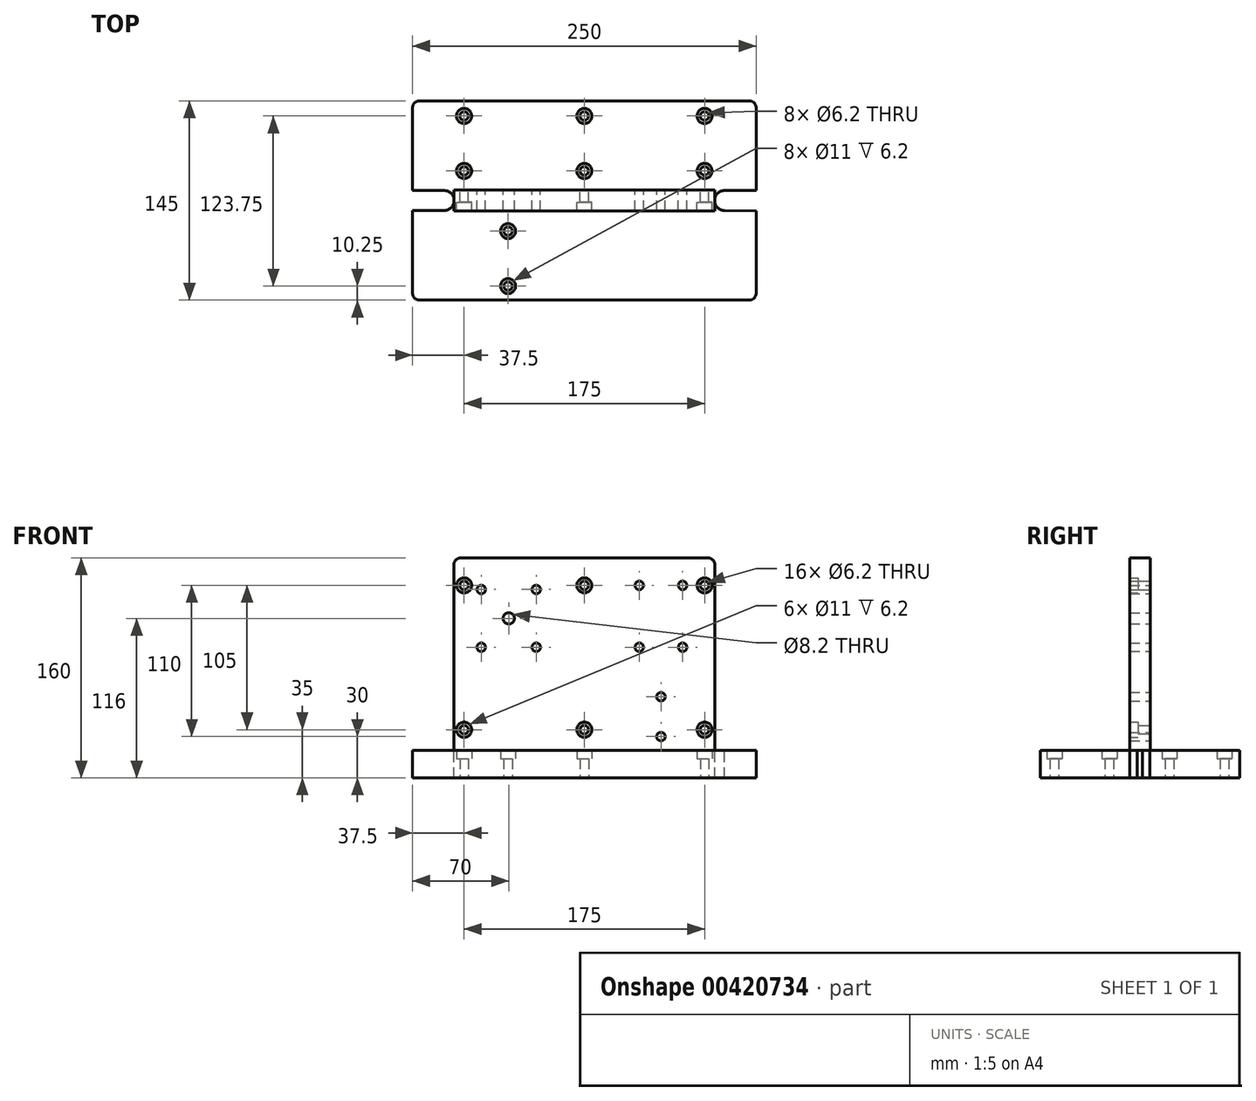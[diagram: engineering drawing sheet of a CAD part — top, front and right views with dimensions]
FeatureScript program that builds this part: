
annotation { "Feature Type Name" : "Feature", "Feature Type Description" : "" }
export const myFeature = defineFeature(function(context is Context, id is Id, definition is map)
    precondition{}
    {
        {
            var Q0;
            Q0=qCreatedBy(makeId("Front.planeOp"),FACE);
            var sketch = newSketch(context, id + "F0", { "sketchPlane" : qUnion([Q0])});
            skLineSegment(sketch, "E0", {"start": v(0, 0) * mm, "end": v(0, 140) * mm});
            skLineSegment(sketch, "E1", {"start": v(0, 140) * mm, "end": v(190, 140) * mm});
            skLineSegment(sketch, "E2", {"start": v(190, 140) * mm, "end": v(190, 0) * mm});
            skLineSegment(sketch, "E3", {"start": v(190, 0) * mm, "end": v(0, 0) * mm});
            skLineSegment(sketch, "E4", {"start": v(0, 0) * mm, "end": v(7.5, 0) * mm});
            skLineSegment(sketch, "E5", {"start": v(7.5, 0) * mm, "end": v(7.5, 15) * mm});
            skLineSegment(sketch, "E6", {"start": v(7.5, 15) * mm, "end": v(7.5, 120) * mm});
            skLineSegment(sketch, "E7", {"start": v(0, 0) * mm, "end": v(20, 0) * mm});
            skLineSegment(sketch, "E8", {"start": v(20, 0) * mm, "end": v(20, 75) * mm});
            skLineSegment(sketch, "E9", {"start": v(20, 75) * mm, "end": v(60, 75) * mm});
            skLineSegment(sketch, "E10", {"start": v(150.75, 75) * mm, "end": v(135, 75) * mm});
            skLineSegment(sketch, "E11.MirrorCS", {"start": v(150.75, 75) * mm, "end": v(166.5, 75) * mm});
            skLineSegment(sketch, "E12.MirrorCS", {"start": v(150.75, 120) * mm, "end": v(135, 120) * mm});
            skLineSegment(sketch, "E13.MirrorCS", {"start": v(150.75, 120) * mm, "end": v(166.5, 120) * mm});
            skLineSegment(sketch, "E14", {"start": v(95, 140) * mm, "end": v(95, 132.56) * mm});
            skLineSegment(sketch, "E15.MirrorCS", {"start": v(182.5, 15) * mm, "end": v(182.5, 120) * mm});
            skPoint(sketch, "E16.endSnap0", {"position": v(40, 75) * mm});
            skLineSegment(sketch, "E17", {"start": v(135, 75) * mm, "end": v(135, 0) * mm});
            skLineSegment(sketch, "E18", {"start": v(135, 75) * mm, "end": v(135, 120) * mm});
            skLineSegment(sketch, "E19", {"start": v(20, 117) * mm, "end": v(60, 117) * mm});
            skLineSegment(sketch, "E20", {"start": v(40, 117) * mm, "end": v(40, 96) * mm});
            skPoint(sketch, "E20.endSnap0", {"position": v(20, 96) * mm});
            skLineSegment(sketch, "E21", {"start": v(20, 75) * mm, "end": v(20, 117) * mm});
            skLineSegment(sketch, "E22", {"start": v(60, 75) * mm, "end": v(135, 75) * mm});
            skLineSegment(sketch, "E23", {"start": v(150.75, 75) * mm, "end": v(150.75, 0) * mm});
            skLineSegment(sketch, "E24", {"start": v(150.75, 0) * mm, "end": v(150.75, 10) * mm});
            skLineSegment(sketch, "E25", {"start": v(150.75, 10) * mm, "end": v(150.75, 39) * mm});
            skLineSegment(sketch, "E26", {"start": v(7.5, 120) * mm, "end": v(95, 120) * mm});
            skLineSegment(sketch, "E27", {"start": v(7.5, 15) * mm, "end": v(95, 15) * mm});
            skPoint(sketch, "E27.endSnap0", {"position": v(95, 0) * mm});
            skSolve(sketch);
        }
        {
            var Q0;
            {var subQ1=sQuery(id+"F0.wireOp",EDGE,"E0");Q0=makeQuery(id+"F0.imprint","IMPRINT",FACE,{"disambiguationData":[TD([[makeQuery(id+"F0.imprint","IMPRINT",EDGE,{"derivedFrom":subQ1}),-1.0]])]});}
            var Q1;
            {var subQ0=sQuery(id+"F0.wireOp",EDGE,"E8");Q1=makeQuery(id+"F0.imprint","IMPRINT",FACE,{"disambiguationData":[TD([[makeQuery(id+"F0.imprint","IMPRINT",EDGE,{"derivedFrom":subQ0}),-1.0]])]});}
            var Q2;
            Q2=makeQuery(id+"F0.imprint","IMPRINT",FACE,{"disambiguationData":[TD([[makeQuery(id+"F0.imprint","IMPRINT",EDGE,{"derivedFrom":sQuery(id+"F0.wireOp",EDGE,"E10")}),1.0]])]});
            var Q3;
            {var subQ0=sQuery(id+"F0.wireOp",EDGE,"E5");Q3=makeQuery(id+"F0.imprint","IMPRINT",FACE,{"disambiguationData":[TD([[makeQuery(id+"F0.imprint","IMPRINT",EDGE,{"derivedFrom":subQ0}),-1.0]])]});}
            extrude(context, id + "F1", {"entities" : qUnion([Q0, Q1, Q2, Q3]), "oppositeDirection" : true, "depth" : 15 * mm});
        }
        {
            var Q0;
            Q0=sQuery(id+"F0.wireOp",VERTEX,"34mdLmB8-NYQB-JZsu-nvt2-5NjCd41thSz9.end");
            var Q1;
            Q1=sQuery(id+"F0.wireOp",VERTEX,"34mdLmB8-NYQB-JZsu-nvt2-5NjCd41thSz9.start");
            var Q2;
            Q2=sQuery(id+"F0.wireOp",VERTEX,"sVGx68N3-lHx0-SeU1-Wsyp-G0nHdIK6jY9Y.start");
            var Q3;
            Q3=sQuery(id+"F0.wireOp",VERTEX,"E9.start");
            var Q4;
            Q4=sQuery(id+"F0.wireOp",VERTEX,"E10.end");
            var Q5;
            Q5=sQuery(id+"F0.wireOp",VERTEX,"E11.MirrorCS.end");
            var Q6;
            Q6=sQuery(id+"F0.wireOp",VERTEX,"E13.MirrorCS.end");
            var Q7;
            Q7=sQuery(id+"F0.wireOp",VERTEX,"E12.MirrorCS.end");
            var Q8;
            Q8=sQuery(id+"F0.wireOp",VERTEX,"E21.end");
            var Q9;
            Q9=sQuery(id+"F0.wireOp",VERTEX,"E9.end");
            var Q10;
            Q10=sQuery(id+"F0.wireOp",VERTEX,"E19.end");
            var Q11;
            Q11=sQuery(id+"F0.wireOp",VERTEX,"BHiPy3Hi-77jz-DfpR-rVcZ-a86G7vlrGmI7.start");
            var Q12;
            Q12=sQuery(id+"F0.wireOp",VERTEX,"BHiPy3Hi-77jz-DfpR-rVcZ-a86G7vlrGmI7.end");
            var Q13;
            Q13=makeQuery(id+"F1.opExtrude","SWEPT_BODY",BODY,{"disambiguationData":[OSD([sQuery(id+"F0.wireOp",EDGE,"E0"),sQuery(id+"F0.wireOp",EDGE,"E1"),sQuery(id+"F0.wireOp",EDGE,"E2"),sQuery(id+"F0.wireOp",EDGE,"E3"),sQuery(id+"F0.wireOp",EDGE,"E7")])]});
            hole(context, id + "F2", {"style" : HoleStyle.SIMPLE, "endStyle" : HoleEndStyle.THROUGH, "holeDiameter" : 6.2 * mm, "isTappedThrough" : true, "tappedDepth" : 12 * mm, "tapClearance" : 3, "locations" : qUnion([Q0, Q1, Q2, Q3, Q4, Q5, Q6, Q7, Q8, Q9, Q10, Q11, Q12]), "scope" : qUnion([Q13]), "startStyle" : HoleStartStyle.PART});
        }
        {
            var Q0;
            Q0=sQuery(id+"F0.wireOp",VERTEX,"D5USdWYK-PwDX-QjbQ-VQpl-hIfxQhAHhKJj.end");
            var Q1;
            Q1=sQuery(id+"F0.wireOp",VERTEX,"E20.end");
            var Q2;
            Q2=makeQuery(id+"F1.opExtrude","SWEPT_BODY",BODY,{"disambiguationData":[OSD([sQuery(id+"F0.wireOp",EDGE,"E0"),sQuery(id+"F0.wireOp",EDGE,"E1"),sQuery(id+"F0.wireOp",EDGE,"E2"),sQuery(id+"F0.wireOp",EDGE,"E3"),sQuery(id+"F0.wireOp",EDGE,"E7")])]});
            hole(context, id + "F3", {"style" : HoleStyle.SIMPLE, "endStyle" : HoleEndStyle.THROUGH, "holeDiameter" : 8.2 * mm, "isTappedThrough" : true, "tappedDepth" : 12 * mm, "tapClearance" : 3, "locations" : qUnion([Q0, Q1]), "scope" : qUnion([Q2]), "startStyle" : HoleStartStyle.PART});
        }
        {
            var Q0;
            Q0=makeQuery(id+"F1.opExtrude","SWEPT_FACE",FACE,{"disambiguationData":[OSD([sQuery(id+"F0.wireOp",EDGE,"E3"),sQuery(id+"F0.wireOp",EDGE,"E7")])]});
            var sketch = newSketch(context, id + "F4", { "sketchPlane" : qUnion([Q0])});
            skLineSegment(sketch, "E28", {"start": v(95, 0) * mm, "end": v(95, 65) * mm});
            skLineSegment(sketch, "E29", {"start": v(95, 65) * mm, "end": v(-30, 65) * mm});
            skLineSegment(sketch, "E30", {"start": v(-30, 65) * mm, "end": v(-30, -7.5) * mm});
            skPoint(sketch, "E30.endSnap0", {"position": v(0, -7.5) * mm});
            skLineSegment(sketch, "E31.MirrorCS", {"start": v(95, 65) * mm, "end": v(220, 65) * mm});
            skLineSegment(sketch, "E32.MirrorCS", {"start": v(220, 65) * mm, "end": v(220, -7.5) * mm});
            skLineSegment(sketch, "E33.MirrorCS", {"start": v(-30, -80) * mm, "end": v(-30, -7.5) * mm});
            skLineSegment(sketch, "E34.MirrorCS", {"start": v(95, -80) * mm, "end": v(-30, -80) * mm});
            skLineSegment(sketch, "E35.MirrorCS", {"start": v(95, -80) * mm, "end": v(220, -80) * mm});
            skLineSegment(sketch, "E36.MirrorCS", {"start": v(220, -80) * mm, "end": v(220, -7.5) * mm});
            skLineSegment(sketch, "E37", {"start": v(-30, -7.5) * mm, "end": v(-14.25, -7.5) * mm});
            skArc(sketch, "E38", {"start": v(-7, -14.75) * mm, "mid": v(0.25, -7.5) * mm, "end": v(-7, -0.25) * mm});
            skLineSegment(sketch, "E39", {"start": v(-7, -7.5) * mm, "end": v(-7, -14.75) * mm});
            skLineSegment(sketch, "E40", {"start": v(-7, -14.75) * mm, "end": v(-30, -14.75) * mm});
            skLineSegment(sketch, "E41.MirrorCS", {"start": v(-7, -0.25) * mm, "end": v(-30, -0.25) * mm});
            skArc(sketch, "E42.MirrorCS", {"start": v(197, -14.75) * mm, "mid": v(189.75, -7.5) * mm, "end": v(197, -0.25) * mm});
            skLineSegment(sketch, "E43.MirrorCS", {"start": v(197, -14.75) * mm, "end": v(220, -14.75) * mm});
            skLineSegment(sketch, "E44", {"start": v(7.5, -29) * mm, "end": v(7.5, -29) * mm});
            skLineSegment(sketch, "E45", {"start": v(7.5, -29) * mm, "end": v(7.5, -69) * mm});
            skLineSegment(sketch, "E46", {"start": v(197, -0.25) * mm, "end": v(220, 0) * mm});
            skLineSegment(sketch, "E47", {"start": v(7.5, -69) * mm, "end": v(182.5, -69) * mm});
            skLineSegment(sketch, "E48", {"start": v(182.5, -15) * mm, "end": v(182.5, 0) * mm});
            skLineSegment(sketch, "E49", {"start": v(182.5, 0) * mm, "end": v(182.5, -15) * mm});
            skCircle(sketch, "E50", {"center": v(7.5, -69) * mm, "radius": 3 * mm});
            skCircle(sketch, "E51", {"center": v(7.5, -69) * mm, "radius": 6 * mm});
            skCircle(sketch, "E52.MirrorC", {"center": v(182.5, -69) * mm, "radius": 6 * mm});
            skCircle(sketch, "E53.MirrorC", {"center": v(182.5, -69) * mm, "radius": 3 * mm});
            skLineSegment(sketch, "E54", {"start": v(7.5, -49) * mm, "end": v(29.1, -49) * mm});
            skPoint(sketch, "E54.endSnap0", {"position": v(7.5, -49) * mm});
            skCircle(sketch, "E55.MirrorC", {"center": v(7.5, -29) * mm, "radius": 6 * mm});
            skCircle(sketch, "E56.MirrorC", {"center": v(7.5, -29) * mm, "radius": 3 * mm});
            skCircle(sketch, "E57.MirrorC", {"center": v(182.5, -29) * mm, "radius": 6 * mm});
            skCircle(sketch, "E58.MirrorC", {"center": v(182.5, -29) * mm, "radius": 3 * mm});
            skLineSegment(sketch, "E59", {"start": v(95, -69) * mm, "end": v(95, -29) * mm});
            skLineSegment(sketch, "E60", {"start": v(7.5, -29) * mm, "end": v(7.5, 0) * mm});
            skLineSegment(sketch, "E61", {"start": v(7.5, 0) * mm, "end": v(39.5, 0) * mm});
            skLineSegment(sketch, "E62", {"start": v(39.5, 0) * mm, "end": v(39.5, -29) * mm});
            skLineSegment(sketch, "E63", {"start": v(39.5, -29) * mm, "end": v(39.5, 14.75) * mm});
            skLineSegment(sketch, "E64", {"start": v(39.5, 14.75) * mm, "end": v(39.5, 54.75) * mm});
            skSolve(sketch);
        }
        {
            var Q0;
            {var subQ0=sQuery(id+"F4.wireOp",EDGE,"E51");var subQ1=sQuery(id+"F4.wireOp",EDGE,"E45");var subQ2=makeQuery(id+"F4.imprint","INTERSECT",VERTEX,{"derivedFrom":[subQ1,subQ0]});Q0=makeQuery(id+"F4.imprint","IMPRINT",FACE,{"disambiguationData":[TD([[makeQuery(id+"F4.imprint","IMPRINT",EDGE,{"disambiguationData":[TD([[subQ2,-1.0]])],"derivedFrom":subQ1}),-1.0]])]});}
            var Q1;
            {var subQ0=sQuery(id+"F4.wireOp",EDGE,"E51");var subQ1=sQuery(id+"F4.wireOp",EDGE,"E45");var subQ2=makeQuery(id+"F4.imprint","INTERSECT",VERTEX,{"derivedFrom":[subQ1,subQ0]});Q1=makeQuery(id+"F4.imprint","IMPRINT",FACE,{"disambiguationData":[TD([[makeQuery(id+"F4.imprint","IMPRINT",EDGE,{"disambiguationData":[TD([[subQ2,-1.0]])],"derivedFrom":subQ1}),1.0]])]});}
            var Q2;
            Q2=makeQuery(id+"F4.imprint","IMPRINT",FACE,{"disambiguationData":[TD([[makeQuery(id+"F4.imprint","IMPRINT",EDGE,{"derivedFrom":sQuery(id+"F4.wireOp",EDGE,"E52.MirrorC")}),-1.0]])]});
            var Q3;
            {var subQ0=sQuery(id+"F4.wireOp",EDGE,"E51");var subQ1=sQuery(id+"F4.wireOp",EDGE,"E47");var subQ2=makeQuery(id+"F4.imprint","INTERSECT",VERTEX,{"derivedFrom":[subQ1,subQ0]});Q3=makeQuery(id+"F4.imprint","IMPRINT",FACE,{"disambiguationData":[TD([[makeQuery(id+"F4.imprint","IMPRINT",EDGE,{"disambiguationData":[TD([[subQ2,1.0]])],"derivedFrom":subQ1}),-1.0]])]});}
            var Q4;
            {var subQ0=sQuery(id+"F4.wireOp",EDGE,"E51");var subQ1=sQuery(id+"F4.wireOp",EDGE,"E47");var subQ2=makeQuery(id+"F4.imprint","INTERSECT",VERTEX,{"derivedFrom":[subQ1,subQ0]});Q4=makeQuery(id+"F4.imprint","IMPRINT",FACE,{"disambiguationData":[TD([[makeQuery(id+"F4.imprint","IMPRINT",EDGE,{"disambiguationData":[TD([[subQ2,1.0]])],"derivedFrom":subQ1}),-1.0]])]});}
            var Q5;
            {var subQ0=sQuery(id+"F4.wireOp",EDGE,"E51");var subQ1=sQuery(id+"F4.wireOp",EDGE,"E47");var subQ2=makeQuery(id+"F4.imprint","INTERSECT",VERTEX,{"derivedFrom":[subQ1,subQ0]});Q5=makeQuery(id+"F4.imprint","IMPRINT",FACE,{"disambiguationData":[TD([[makeQuery(id+"F4.imprint","IMPRINT",EDGE,{"disambiguationData":[TD([[subQ2,1.0]])],"derivedFrom":subQ1}),1.0]])]});}
            var Q6;
            {var subQ0=sQuery(id+"F4.wireOp",EDGE,"E56.MirrorC");var subQ1=sQuery(id+"F4.wireOp",EDGE,"E45");var subQ2=makeQuery(id+"F4.imprint","INTERSECT",VERTEX,{"derivedFrom":[subQ1,subQ0]});Q6=makeQuery(id+"F4.imprint","IMPRINT",FACE,{"disambiguationData":[TD([[makeQuery(id+"F4.imprint","IMPRINT",EDGE,{"disambiguationData":[TD([[subQ2,-1.0]])],"derivedFrom":subQ1}),1.0]])]});}
            var Q7;
            {var subQ0=sQuery(id+"F4.wireOp",EDGE,"E58.MirrorC");var subQ1=sQuery(id+"F4.wireOp",EDGE,"E49");var subQ2=makeQuery(id+"F4.imprint","INTERSECT",VERTEX,{"derivedFrom":[subQ1,subQ0]});Q7=makeQuery(id+"F4.imprint","IMPRINT",FACE,{"disambiguationData":[TD([[makeQuery(id+"F4.imprint","IMPRINT",EDGE,{"disambiguationData":[TD([[subQ2,-1.0]])],"derivedFrom":subQ1}),-1.0]])]});}
            var Q8;
            {var subQ0=sQuery(id+"F4.wireOp",EDGE,"E56.MirrorC");var subQ1=sQuery(id+"F4.wireOp",EDGE,"mPhaeWDJ-Nzgz-2L0b-y6cd-HvV1nDqMggiO");var subQ2=makeQuery(id+"F4.imprint","INTERSECT",VERTEX,{"derivedFrom":[subQ1,subQ0]});Q8=makeQuery(id+"F4.imprint","IMPRINT",FACE,{"disambiguationData":[TD([[makeQuery(id+"F4.imprint","IMPRINT",EDGE,{"disambiguationData":[TD([[subQ2,-1.0]])],"derivedFrom":subQ1}),-1.0]])]});}
            var Q9;
            {var subQ0=sQuery(id+"F4.wireOp",EDGE,"E56.MirrorC");var subQ1=sQuery(id+"F4.wireOp",EDGE,"mPhaeWDJ-Nzgz-2L0b-y6cd-HvV1nDqMggiO");var subQ2=makeQuery(id+"F4.imprint","INTERSECT",VERTEX,{"derivedFrom":[subQ1,subQ0]});Q9=makeQuery(id+"F4.imprint","IMPRINT",FACE,{"disambiguationData":[TD([[makeQuery(id+"F4.imprint","IMPRINT",EDGE,{"disambiguationData":[TD([[subQ2,-1.0]])],"derivedFrom":subQ1}),1.0]])]});}
            var Q10;
            {var subQ0=sQuery(id+"F4.wireOp",EDGE,"E57.MirrorC");var subQ1=sQuery(id+"F4.wireOp",EDGE,"6e4d2df1-713c-46b8-b697-84e0066bc4920.MirrorCS");var subQ2=makeQuery(id+"F4.imprint","INTERSECT",VERTEX,{"derivedFrom":[subQ1,subQ0]});Q10=makeQuery(id+"F4.imprint","IMPRINT",FACE,{"disambiguationData":[TD([[makeQuery(id+"F4.imprint","IMPRINT",EDGE,{"disambiguationData":[TD([[subQ2,-1.0]])],"derivedFrom":subQ1}),1.0]])]});}
            var Q11;
            {var subQ0=sQuery(id+"F4.wireOp",EDGE,"E57.MirrorC");var subQ1=sQuery(id+"F4.wireOp",EDGE,"6e4d2df1-713c-46b8-b697-84e0066bc4920.MirrorCS");var subQ2=makeQuery(id+"F4.imprint","INTERSECT",VERTEX,{"derivedFrom":[subQ1,subQ0]});Q11=makeQuery(id+"F4.imprint","IMPRINT",FACE,{"disambiguationData":[TD([[makeQuery(id+"F4.imprint","IMPRINT",EDGE,{"disambiguationData":[TD([[subQ2,-1.0]])],"derivedFrom":subQ1}),-1.0]])]});}
            var Q12;
            {var subQ18=sQuery(id+"F4.wireOp",EDGE,"E34.MirrorCS");Q12=makeQuery(id+"F4.imprint","IMPRINT",FACE,{"disambiguationData":[TD([[makeQuery(id+"F4.imprint","IMPRINT",EDGE,{"derivedFrom":subQ18}),-1.0]])]});}
            var Q13;
            {var subQ6=sQuery(id+"F4.wireOp",EDGE,"E28");Q13=makeQuery(id+"F4.imprint","IMPRINT",FACE,{"disambiguationData":[TD([[makeQuery(id+"F4.imprint","IMPRINT",EDGE,{"derivedFrom":subQ6}),1.0]])]});}
            var Q14;
            {var subQ8=sQuery(id+"F4.wireOp",EDGE,"E28");Q14=makeQuery(id+"F4.imprint","IMPRINT",FACE,{"disambiguationData":[TD([[makeQuery(id+"F4.imprint","IMPRINT",EDGE,{"derivedFrom":subQ8}),-1.0]])]});}
            var Q15;
            {var subQ0=sQuery(id+"F4.wireOp",EDGE,"E57.MirrorC");var subQ1=sQuery(id+"F4.wireOp",EDGE,"E49");var subQ2=makeQuery(id+"F4.imprint","INTERSECT",VERTEX,{"derivedFrom":[subQ1,subQ0]});Q15=makeQuery(id+"F4.imprint","IMPRINT",FACE,{"disambiguationData":[TD([[makeQuery(id+"F4.imprint","IMPRINT",EDGE,{"disambiguationData":[TD([[subQ2,-1.0]])],"derivedFrom":subQ1}),-1.0]])]});}
            var Q16;
            {var subQ0=sQuery(id+"F4.wireOp",EDGE,"E57.MirrorC");var subQ1=sQuery(id+"F4.wireOp",EDGE,"6e4d2df1-713c-46b8-b697-84e0066bc4920.MirrorCS");var subQ2=makeQuery(id+"F4.imprint","INTERSECT",VERTEX,{"derivedFrom":[subQ1,subQ0]});Q16=makeQuery(id+"F4.imprint","IMPRINT",FACE,{"disambiguationData":[TD([[makeQuery(id+"F4.imprint","IMPRINT",EDGE,{"disambiguationData":[TD([[subQ2,1.0]])],"derivedFrom":subQ0}),-1.0]])]});}
            var Q17;
            {var subQ4=sQuery(id+"F4.wireOp",EDGE,"E55.MirrorC");var subQ12=sQuery(id+"F4.wireOp",EDGE,"mPhaeWDJ-Nzgz-2L0b-y6cd-HvV1nDqMggiO");var subQ14=makeQuery(id+"F4.imprint","INTERSECT",VERTEX,{"derivedFrom":[subQ12,subQ4]});Q17=makeQuery(id+"F4.imprint","IMPRINT",FACE,{"disambiguationData":[TD([[makeQuery(id+"F4.imprint","IMPRINT",EDGE,{"disambiguationData":[TD([[subQ14,1.0]])],"derivedFrom":subQ4}),1.0]])]});}
            var Q18;
            {var subQ0=sQuery(id+"F4.wireOp",EDGE,"E46");Q18=makeQuery(id+"F4.imprint","IMPRINT",FACE,{"disambiguationData":[TD([[makeQuery(id+"F4.imprint","IMPRINT",EDGE,{"derivedFrom":subQ0}),1.0]])]});}
            var Q19;
            {var subQ0=sQuery(id+"F4.wireOp",EDGE,"E41.MirrorCS");Q19=makeQuery(id+"F4.imprint","IMPRINT",FACE,{"disambiguationData":[TD([[makeQuery(id+"F4.imprint","IMPRINT",EDGE,{"derivedFrom":subQ0}),-1.0]])]});}
            extrude(context, id + "F5", {"entities" : qUnion([Q0, Q1, Q2, Q3, Q4, Q5, Q6, Q7, Q8, Q9, Q10, Q11, Q12, Q13, Q14, Q15, Q16, Q17, Q18, Q19]), "depth" : 15 * mm});
        }
        {
            var Q0;
            {var subQ0=sQuery(id+"F4.wireOp",EDGE,"E40");Q0=makeQuery(id+"F4.imprint","IMPRINT",FACE,{"disambiguationData":[TD([[makeQuery(id+"F4.imprint","IMPRINT",EDGE,{"derivedFrom":subQ0}),-1.0]])]});}
            var Q1;
            {var subQ0=sQuery(id+"F4.wireOp",EDGE,"E43.MirrorCS");Q1=makeQuery(id+"F4.imprint","IMPRINT",FACE,{"disambiguationData":[TD([[makeQuery(id+"F4.imprint","IMPRINT",EDGE,{"derivedFrom":subQ0}),1.0]])]});}
            var Q2;
            {var subQ0=sQuery(id+"F4.wireOp",EDGE,"7bHRVPem-sjBZ-Ug8A-odx3-xiCNbKq1Zb4v");var subQ3=sQuery(id+"F4.wireOp",EDGE,"E38");var subQ4=makeQuery(id+"F4.imprint","INTERSECT",VERTEX,{"derivedFrom":[subQ0,subQ3]});Q2=makeQuery(id+"F4.imprint","IMPRINT",FACE,{"disambiguationData":[TD([[makeQuery(id+"F4.imprint","IMPRINT",EDGE,{"disambiguationData":[TD([[subQ4,1.0]])],"derivedFrom":subQ0}),1.0]])]});}
            var Q3;
            {var subQ0=sQuery(id+"F4.wireOp",EDGE,"7bHRVPem-sjBZ-Ug8A-odx3-xiCNbKq1Zb4v");var subQ3=sQuery(id+"F4.wireOp",EDGE,"E38");var subQ4=makeQuery(id+"F4.imprint","INTERSECT",VERTEX,{"derivedFrom":[subQ0,subQ3]});Q3=makeQuery(id+"F4.imprint","IMPRINT",FACE,{"disambiguationData":[TD([[makeQuery(id+"F4.imprint","IMPRINT",EDGE,{"disambiguationData":[TD([[subQ4,1.0]])],"derivedFrom":subQ0}),-1.0]])]});}
            var Q4;
            {var subQ0=sQuery(id+"F4.wireOp",EDGE,"E42.MirrorCS");var subQ1=makeQuery(id+"F1.opExtrude","SWEPT_EDGE",EDGE,{"disambiguationData":[OSD([sQuery(id+"F0.wireOp",EDGE,"E2"),sQuery(id+"F0.wireOp",EDGE,"E3")])]});var subQ2=makeQuery(id+"F4.imprint","INTERSECT",VERTEX,{"disambiguationData":[OD(0.0)],"derivedFrom":[subQ1,subQ0]});Q4=makeQuery(id+"F4.imprint","IMPRINT",FACE,{"disambiguationData":[TD([[makeQuery(id+"F4.imprint","IMPRINT",EDGE,{"disambiguationData":[TD([[subQ2,1.0]])],"derivedFrom":subQ0}),-1.0]])]});}
            extrude(context, id + "F6", {"entities" : qUnion([Q0, Q1, Q2, Q3, Q4]), "operationType" : NewBodyOperationType.REMOVE, "depth" : 25 * mm});
        }
        {
            var Q0;
            Q0=makeQuery(id+"F5.opExtrude","CAP_EDGE",EDGE,{"disambiguationData":[OSD([sQuery(id+"F4.wireOp",EDGE,"E29"),sQuery(id+"F4.wireOp",EDGE,"E31.MirrorCS")])],"isStart":true});
            var Q1;
            {var subQ0=sQuery(id+"F4.wireOp",EDGE,"E33.MirrorCS");var subQ2=sQuery(id+"F4.wireOp",EDGE,"E30");Q1=makeQuery(id+"F6.boolean.opBoolean","SPLIT",EDGE,{"disambiguationData":[TD([makeQuery(id+"F6.opExtrude","SWEPT_FACE",FACE,{"disambiguationData":[OSD([sQuery(id+"F4.wireOp",EDGE,"E41.MirrorCS")])]})])],"derivedFrom":makeQuery(id+"F5.opExtrude","CAP_EDGE",EDGE,{"disambiguationData":[OSD([subQ2,subQ0])],"isStart":true})});}
            var Q2;
            {var subQ2=sQuery(id+"F4.wireOp",EDGE,"E33.MirrorCS");var subQ3=sQuery(id+"F4.wireOp",EDGE,"E30");Q2=makeQuery(id+"F6.boolean.opBoolean","SPLIT",EDGE,{"disambiguationData":[TD([makeQuery(id+"F6.opExtrude","SWEPT_FACE",FACE,{"disambiguationData":[OSD([sQuery(id+"F4.wireOp",EDGE,"E40")])]})])],"derivedFrom":makeQuery(id+"F5.opExtrude","CAP_EDGE",EDGE,{"disambiguationData":[OSD([subQ3,subQ2])],"isStart":true})});}
            var Q3;
            Q3=makeQuery(id+"F5.opExtrude","CAP_EDGE",EDGE,{"disambiguationData":[OSD([sQuery(id+"F4.wireOp",EDGE,"E34.MirrorCS"),sQuery(id+"F4.wireOp",EDGE,"E35.MirrorCS")])],"isStart":true});
            var Q4;
            {var subQ0=sQuery(id+"F4.wireOp",EDGE,"E36.MirrorCS");var subQ1=sQuery(id+"F4.wireOp",EDGE,"E32.MirrorCS");Q4=makeQuery(id+"F6.boolean.opBoolean","SPLIT",EDGE,{"disambiguationData":[TD([makeQuery(id+"F6.opExtrude","SWEPT_FACE",FACE,{"disambiguationData":[OSD([sQuery(id+"F4.wireOp",EDGE,"6e4d2df1-713c-46b8-b697-84e0066bc4920.MirrorCS")])]})])],"derivedFrom":makeQuery(id+"F5.opExtrude","CAP_EDGE",EDGE,{"disambiguationData":[OSD([subQ1,subQ0])],"isStart":true})});}
            var Q5;
            {var subQ0=sQuery(id+"F4.wireOp",EDGE,"E36.MirrorCS");var subQ3=sQuery(id+"F4.wireOp",EDGE,"E32.MirrorCS");Q5=makeQuery(id+"F6.boolean.opBoolean","SPLIT",EDGE,{"disambiguationData":[TD([makeQuery(id+"F6.opExtrude","SWEPT_FACE",FACE,{"disambiguationData":[OSD([sQuery(id+"F4.wireOp",EDGE,"E43.MirrorCS")])]})])],"derivedFrom":makeQuery(id+"F5.opExtrude","CAP_EDGE",EDGE,{"disambiguationData":[OSD([subQ3,subQ0])],"isStart":true})});}
            var Q6;
            Q6=makeQuery(id+"F5.opExtrude","SWEPT_EDGE",EDGE,{"disambiguationData":[OSD([sQuery(id+"F4.wireOp",EDGE,"E29"),sQuery(id+"F4.wireOp",EDGE,"E30")])]});
            var Q7;
            Q7=makeQuery(id+"F5.opExtrude","SWEPT_EDGE",EDGE,{"disambiguationData":[OSD([sQuery(id+"F4.wireOp",EDGE,"E33.MirrorCS"),sQuery(id+"F4.wireOp",EDGE,"E34.MirrorCS")])]});
            var Q8;
            Q8=makeQuery(id+"F5.opExtrude","SWEPT_EDGE",EDGE,{"disambiguationData":[OSD([sQuery(id+"F4.wireOp",EDGE,"E35.MirrorCS"),sQuery(id+"F4.wireOp",EDGE,"E36.MirrorCS")])]});
            var Q9;
            Q9=makeQuery(id+"F5.opExtrude","SWEPT_EDGE",EDGE,{"disambiguationData":[OSD([sQuery(id+"F4.wireOp",EDGE,"E31.MirrorCS"),sQuery(id+"F4.wireOp",EDGE,"E32.MirrorCS")])]});
            var Q10;
            {var subQ0=sQuery(id+"F4.wireOp",EDGE,"E36.MirrorCS");var subQ1=sQuery(id+"F4.wireOp",EDGE,"E32.MirrorCS");Q10=makeQuery(id+"F6.boolean.opBoolean","SPLIT",EDGE,{"disambiguationData":[TD([makeQuery(id+"F6.opExtrude","SWEPT_FACE",FACE,{"disambiguationData":[OSD([sQuery(id+"F4.wireOp",EDGE,"E46")])]})])],"derivedFrom":makeQuery(id+"F5.opExtrude","CAP_EDGE",EDGE,{"disambiguationData":[OSD([subQ1,subQ0])],"isStart":true})});}
            fillet(context, id + "F7", {"entities" : qUnion([Q0, Q1, Q2, Q3, Q4, Q5, Q6, Q7, Q8, Q9, Q10]), "radius" : 5 * mm, "tangentPropagation" : true, "allowEdgeOverflow" : false});
        }
        {
            var Q0;
            Q0=makeQuery(id+"F1.opExtrude","SWEPT_EDGE",EDGE,{"disambiguationData":[OSD([sQuery(id+"F0.wireOp",EDGE,"E0"),sQuery(id+"F0.wireOp",EDGE,"E1")])]});
            var Q1;
            Q1=makeQuery(id+"F1.opExtrude","SWEPT_EDGE",EDGE,{"disambiguationData":[OSD([sQuery(id+"F0.wireOp",EDGE,"E1"),sQuery(id+"F0.wireOp",EDGE,"E2")])]});
            fillet(context, id + "F8", {"entities" : qUnion([Q0, Q1]), "radius" : 5 * mm, "tangentPropagation" : true, "allowEdgeOverflow" : false});
        }
        {
            var Q0;
            {var subQ13=sQuery(id+"F4.wireOp",EDGE,"E34.MirrorCS");Q0=makeQuery(id+"F4.imprint","IMPRINT",FACE,{"disambiguationData":[TD([[makeQuery(id+"F4.imprint","IMPRINT",EDGE,{"derivedFrom":subQ13}),-1.0]])]});}
            cPlane(context, id + "F9", {"entities" : qUnion([Q0]), "cplaneType" : CPlaneType.OFFSET, "offset" : 10 * mm, "width" : 150 * mm, "height" : 150 * mm});
        }
        {
            var Q0;
            Q0=makeQuery(id+"Fad2b0gEey9Uvx4_2.opExtrude","CAP_FACE",FACE,{"disambiguationData":[OSD([sQuery(id+"F4.wireOp",EDGE,"E50"),sQuery(id+"F4.wireOp",EDGE,"E51")])],"isStart":false});
            var Q1;
            Q1=makeQuery(id+"Fad2b0gEey9Uvx4_2.opExtrude","CAP_FACE",FACE,{"disambiguationData":[OSD([sQuery(id+"F4.wireOp",EDGE,"E52.MirrorC"),sQuery(id+"F4.wireOp",EDGE,"E53.MirrorC")])],"isStart":false});
            var Q2;
            {var subQ0=sQuery(id+"F4.wireOp",EDGE,"E51");var subQ1=sQuery(id+"F4.wireOp",EDGE,"E47");var subQ2=makeQuery(id+"F4.imprint","INTERSECT",VERTEX,{"derivedFrom":[subQ1,subQ0]});Q2=makeQuery(id+"F4.imprint","IMPRINT",FACE,{"disambiguationData":[TD([[makeQuery(id+"F4.imprint","IMPRINT",EDGE,{"disambiguationData":[TD([[subQ2,1.0]])],"derivedFrom":subQ1}),-1.0]])]});}
            var Q3;
            {var subQ0=sQuery(id+"F4.wireOp",EDGE,"E51");var subQ1=sQuery(id+"F4.wireOp",EDGE,"E47");var subQ2=makeQuery(id+"F4.imprint","INTERSECT",VERTEX,{"derivedFrom":[subQ1,subQ0]});Q3=makeQuery(id+"F4.imprint","IMPRINT",FACE,{"disambiguationData":[TD([[makeQuery(id+"F4.imprint","IMPRINT",EDGE,{"disambiguationData":[TD([[subQ2,1.0]])],"derivedFrom":subQ1}),1.0]])]});}
            var Q4;
            {var subQ0=sQuery(id+"F4.wireOp",EDGE,"E56.MirrorC");var subQ1=sQuery(id+"F4.wireOp",EDGE,"E45");var subQ2=makeQuery(id+"F4.imprint","INTERSECT",VERTEX,{"derivedFrom":[subQ1,subQ0]});Q4=makeQuery(id+"F4.imprint","IMPRINT",FACE,{"disambiguationData":[TD([[makeQuery(id+"F4.imprint","IMPRINT",EDGE,{"disambiguationData":[TD([[subQ2,-1.0]])],"derivedFrom":subQ1}),1.0]])]});}
            var Q5;
            {var subQ0=sQuery(id+"F4.wireOp",EDGE,"E55.MirrorC");var subQ1=sQuery(id+"F4.wireOp",EDGE,"mPhaeWDJ-Nzgz-2L0b-y6cd-HvV1nDqMggiO");var subQ2=makeQuery(id+"F4.imprint","INTERSECT",VERTEX,{"derivedFrom":[subQ1,subQ0]});Q5=makeQuery(id+"F4.imprint","IMPRINT",FACE,{"disambiguationData":[TD([[makeQuery(id+"F4.imprint","IMPRINT",EDGE,{"disambiguationData":[TD([[subQ2,-1.0]])],"derivedFrom":subQ1}),-1.0]])]});}
            var Q6;
            {var subQ0=sQuery(id+"F4.wireOp",EDGE,"E58.MirrorC");var subQ1=sQuery(id+"F4.wireOp",EDGE,"E49");var subQ2=makeQuery(id+"F4.imprint","INTERSECT",VERTEX,{"derivedFrom":[subQ1,subQ0]});Q6=makeQuery(id+"F4.imprint","IMPRINT",FACE,{"disambiguationData":[TD([[makeQuery(id+"F4.imprint","IMPRINT",EDGE,{"disambiguationData":[TD([[subQ2,-1.0]])],"derivedFrom":subQ1}),-1.0]])]});}
            var Q7;
            {var subQ0=sQuery(id+"F4.wireOp",EDGE,"E58.MirrorC");var subQ1=sQuery(id+"F4.wireOp",EDGE,"6e4d2df1-713c-46b8-b697-84e0066bc4920.MirrorCS");var subQ2=makeQuery(id+"F4.imprint","INTERSECT",VERTEX,{"derivedFrom":[subQ1,subQ0]});Q7=makeQuery(id+"F4.imprint","IMPRINT",FACE,{"disambiguationData":[TD([[makeQuery(id+"F4.imprint","IMPRINT",EDGE,{"disambiguationData":[TD([[subQ2,-1.0]])],"derivedFrom":subQ1}),-1.0]])]});}
            var Q8;
            {var subQ0=sQuery(id+"F4.wireOp",EDGE,"E58.MirrorC");var subQ1=sQuery(id+"F4.wireOp",EDGE,"6e4d2df1-713c-46b8-b697-84e0066bc4920.MirrorCS");var subQ2=makeQuery(id+"F4.imprint","INTERSECT",VERTEX,{"derivedFrom":[subQ1,subQ0]});Q8=makeQuery(id+"F4.imprint","IMPRINT",FACE,{"disambiguationData":[TD([[makeQuery(id+"F4.imprint","IMPRINT",EDGE,{"disambiguationData":[TD([[subQ2,-1.0]])],"derivedFrom":subQ1}),1.0]])]});}
            var Q9;
            {var subQ0=sQuery(id+"F4.wireOp",EDGE,"E55.MirrorC");var subQ1=sQuery(id+"F4.wireOp",EDGE,"mPhaeWDJ-Nzgz-2L0b-y6cd-HvV1nDqMggiO");var subQ2=makeQuery(id+"F4.imprint","INTERSECT",VERTEX,{"derivedFrom":[subQ1,subQ0]});Q9=makeQuery(id+"F4.imprint","IMPRINT",FACE,{"disambiguationData":[TD([[makeQuery(id+"F4.imprint","IMPRINT",EDGE,{"disambiguationData":[TD([[subQ2,-1.0]])],"derivedFrom":subQ1}),1.0]])]});}
            var Q10;
            Q10=makeQuery(id+"Fad2b0gEey9Uvx4_2.opExtrude","CAP_FACE",FACE,{"disambiguationData":[OSD([sQuery(id+"F4.wireOp",EDGE,"E57.MirrorC"),sQuery(id+"F4.wireOp",EDGE,"E58.MirrorC")])],"isStart":false});
            var Q11;
            Q11=makeQuery(id+"Fad2b0gEey9Uvx4_2.opExtrude","CAP_FACE",FACE,{"disambiguationData":[OSD([sQuery(id+"F4.wireOp",EDGE,"E55.MirrorC"),sQuery(id+"F4.wireOp",EDGE,"E56.MirrorC")])],"isStart":false});
            extrude(context, id + "F10", {"entities" : qUnion([Q0, Q1, Q2, Q3, Q4, Q5, Q6, Q7, Q8, Q9, Q10, Q11]), "operationType" : NewBodyOperationType.REMOVE, "oppositeDirection" : true, "depth" : 18 * mm});
        }
        {
            var Q0;
            Q0=sQuery(id+"F0.wireOp",VERTEX,"E6.end");
            var Q1;
            Q1=sQuery(id+"F0.wireOp",VERTEX,"E6.start");
            var Q2;
            Q2=sQuery(id+"F0.wireOp",VERTEX,"E15.MirrorCS.start");
            var Q3;
            Q3=sQuery(id+"F0.wireOp",VERTEX,"E15.MirrorCS.end");
            var Q4;
            Q4=sQuery(id+"F0.wireOp",VERTEX,"E26.end");
            var Q5;
            Q5=sQuery(id+"F0.wireOp",VERTEX,"E27.end");
            var Q6;
            Q6=makeQuery(id+"F1.opExtrude","SWEPT_BODY",BODY,{"disambiguationData":[OSD([sQuery(id+"F0.wireOp",EDGE,"E0"),sQuery(id+"F0.wireOp",EDGE,"E1"),sQuery(id+"F0.wireOp",EDGE,"E2"),sQuery(id+"F0.wireOp",EDGE,"E3"),sQuery(id+"F0.wireOp",EDGE,"E7")])]});
            hole(context, id + "F11", {"style" : HoleStyle.C_BORE, "endStyle" : HoleEndStyle.THROUGH, "holeDiameter" : 6.2 * mm, "cBoreDiameter" : 11 * mm, "cBoreDepth" : 6.2 * mm, "majorDiameter" : 5 * mm, "isTappedThrough" : true, "tappedDepth" : 12 * mm, "tapClearance" : 3, "locations" : qUnion([Q0, Q1, Q2, Q3, Q4, Q5]), "scope" : qUnion([Q6]), "startStyle" : HoleStartStyle.PART});
        }
        {
            var Q0;
            Q0=makeQuery(id+"F5.opExtrude","SWEPT_BODY",BODY,{"disambiguationData":[OSD([sQuery(id+"F0.wireOp",EDGE,"E3"),sQuery(id+"F0.wireOp",EDGE,"E7"),sQuery(id+"F4.wireOp",EDGE,"E49"),sQuery(id+"F4.wireOp",EDGE,"E58.MirrorC")])]});
            deleteBodies(context, id + "F12", {"entities" : qUnion([Q0])});
        }
        {
            var Q0;
            Q0 = qSketchRegion(id + "F4", true);
            var Q1;
            {var subQ0=sQuery(id+"F4.wireOp",EDGE,"E51");var subQ1=sQuery(id+"F4.wireOp",EDGE,"E47");var subQ2=makeQuery(id+"F4.imprint","INTERSECT",VERTEX,{"derivedFrom":[subQ1,subQ0]});Q1=makeQuery(id+"F4.imprint","IMPRINT",FACE,{"disambiguationData":[TD([[makeQuery(id+"F4.imprint","IMPRINT",EDGE,{"disambiguationData":[TD([[subQ2,1.0]])],"derivedFrom":subQ1}),-1.0]])]});}
            var Q2;
            {var subQ0=sQuery(id+"F4.wireOp",EDGE,"E45");var subQ1=sQuery(id+"F4.wireOp",EDGE,"E47");var subQ2=makeQuery(id+"F4.imprint","INTERSECT",VERTEX,{"derivedFrom":[subQ1,subQ0]});Q2=makeQuery(id+"F4.imprint","IMPRINT",FACE,{"disambiguationData":[TD([[makeQuery(id+"F4.imprint","IMPRINT",EDGE,{"disambiguationData":[TD([[subQ2,-1.0]])],"derivedFrom":subQ1}),-1.0]])]});}
            var Q3;
            Q3=makeQuery(id+"F4.imprint","IMPRINT",FACE,{"disambiguationData":[TD([[makeQuery(id+"F4.imprint","IMPRINT",EDGE,{"derivedFrom":sQuery(id+"F4.wireOp",EDGE,"E52.MirrorC")}),-1.0]])]});
            var Q4;
            Q4=makeQuery(id+"F4.imprint","IMPRINT",FACE,{"disambiguationData":[TD([[makeQuery(id+"F4.imprint","IMPRINT",EDGE,{"derivedFrom":sQuery(id+"F4.wireOp",EDGE,"E53.MirrorC")}),-1.0]])]});
            var Q5;
            {var subQ0=sQuery(id+"F4.wireOp",EDGE,"E56.MirrorC");var subQ1=sQuery(id+"F4.wireOp",EDGE,"E45");var subQ2=makeQuery(id+"F4.imprint","INTERSECT",VERTEX,{"derivedFrom":[subQ1,subQ0]});Q5=makeQuery(id+"F4.imprint","IMPRINT",FACE,{"disambiguationData":[TD([[makeQuery(id+"F4.imprint","IMPRINT",EDGE,{"disambiguationData":[TD([[subQ2,-1.0]])],"derivedFrom":subQ1}),1.0]])]});}
            var Q6;
            {var subQ1=sQuery(id+"F4.wireOp",EDGE,"mPhaeWDJ-Nzgz-2L0b-y6cd-HvV1nDqMggiO");var subQ3=sQuery(id+"F4.wireOp",EDGE,"E56.MirrorC");var subQ4=makeQuery(id+"F4.imprint","INTERSECT",VERTEX,{"derivedFrom":[subQ1,subQ3]});Q6=makeQuery(id+"F4.imprint","IMPRINT",FACE,{"disambiguationData":[TD([[makeQuery(id+"F4.imprint","IMPRINT",EDGE,{"disambiguationData":[TD([[subQ4,1.0]])],"derivedFrom":subQ3}),-1.0]])]});}
            var Q7;
            {var subQ0=sQuery(id+"F4.wireOp",EDGE,"E56.MirrorC");var subQ1=sQuery(id+"F4.wireOp",EDGE,"mPhaeWDJ-Nzgz-2L0b-y6cd-HvV1nDqMggiO");var subQ2=makeQuery(id+"F4.imprint","INTERSECT",VERTEX,{"derivedFrom":[subQ1,subQ0]});Q7=makeQuery(id+"F4.imprint","IMPRINT",FACE,{"disambiguationData":[TD([[makeQuery(id+"F4.imprint","IMPRINT",EDGE,{"disambiguationData":[TD([[subQ2,-1.0]])],"derivedFrom":subQ1}),1.0]])]});}
            var Q8;
            {var subQ0=sQuery(id+"F4.wireOp",EDGE,"E56.MirrorC");var subQ1=sQuery(id+"F4.wireOp",EDGE,"mPhaeWDJ-Nzgz-2L0b-y6cd-HvV1nDqMggiO");var subQ2=makeQuery(id+"F4.imprint","INTERSECT",VERTEX,{"derivedFrom":[subQ1,subQ0]});Q8=makeQuery(id+"F4.imprint","IMPRINT",FACE,{"disambiguationData":[TD([[makeQuery(id+"F4.imprint","IMPRINT",EDGE,{"disambiguationData":[TD([[subQ2,-1.0]])],"derivedFrom":subQ1}),-1.0]])]});}
            var Q9;
            {var subQ0=sQuery(id+"F4.wireOp",EDGE,"E57.MirrorC");var subQ1=sQuery(id+"F4.wireOp",EDGE,"6e4d2df1-713c-46b8-b697-84e0066bc4920.MirrorCS");var subQ2=makeQuery(id+"F4.imprint","INTERSECT",VERTEX,{"derivedFrom":[subQ1,subQ0]});Q9=makeQuery(id+"F4.imprint","IMPRINT",FACE,{"disambiguationData":[TD([[makeQuery(id+"F4.imprint","IMPRINT",EDGE,{"disambiguationData":[TD([[subQ2,-1.0]])],"derivedFrom":subQ1}),-1.0]])]});}
            var Q10;
            {var subQ0=sQuery(id+"F4.wireOp",EDGE,"6e4d2df1-713c-46b8-b697-84e0066bc4920.MirrorCS");var subQ3=sQuery(id+"F4.wireOp",EDGE,"E58.MirrorC");var subQ4=makeQuery(id+"F4.imprint","INTERSECT",VERTEX,{"derivedFrom":[subQ0,subQ3]});Q10=makeQuery(id+"F4.imprint","IMPRINT",FACE,{"disambiguationData":[TD([[makeQuery(id+"F4.imprint","IMPRINT",EDGE,{"disambiguationData":[TD([[subQ4,-1.0]])],"derivedFrom":subQ3}),1.0]])]});}
            var Q11;
            {var subQ0=sQuery(id+"F4.wireOp",EDGE,"E51");var subQ1=sQuery(id+"F4.wireOp",EDGE,"E47");var subQ2=makeQuery(id+"F4.imprint","INTERSECT",VERTEX,{"derivedFrom":[subQ1,subQ0]});Q11=makeQuery(id+"F4.imprint","IMPRINT",FACE,{"disambiguationData":[TD([[makeQuery(id+"F4.imprint","IMPRINT",EDGE,{"disambiguationData":[TD([[subQ2,1.0]])],"derivedFrom":subQ1}),1.0]])]});}
            var Q12;
            {var subQ0=sQuery(id+"F4.wireOp",EDGE,"E45");var subQ1=sQuery(id+"F4.wireOp",EDGE,"E47");var subQ2=makeQuery(id+"F4.imprint","INTERSECT",VERTEX,{"derivedFrom":[subQ1,subQ0]});Q12=makeQuery(id+"F4.imprint","IMPRINT",FACE,{"disambiguationData":[TD([[makeQuery(id+"F4.imprint","IMPRINT",EDGE,{"disambiguationData":[TD([[subQ2,-1.0]])],"derivedFrom":subQ1}),1.0]])]});}
            var Q13;
            {var subQ0=sQuery(id+"F4.wireOp",EDGE,"mPhaeWDJ-Nzgz-2L0b-y6cd-HvV1nDqMggiO");var subQ3=sQuery(id+"F4.wireOp",EDGE,"E56.MirrorC");var subQ4=makeQuery(id+"F4.imprint","INTERSECT",VERTEX,{"derivedFrom":[subQ0,subQ3]});Q13=makeQuery(id+"F4.imprint","IMPRINT",FACE,{"disambiguationData":[TD([[makeQuery(id+"F4.imprint","IMPRINT",EDGE,{"disambiguationData":[TD([[subQ4,-1.0]])],"derivedFrom":subQ3}),-1.0]])]});}
            var Q14;
            {var subQ0=sQuery(id+"F4.wireOp",EDGE,"E58.MirrorC");var subQ1=sQuery(id+"F4.wireOp",EDGE,"E49");var subQ2=makeQuery(id+"F4.imprint","INTERSECT",VERTEX,{"derivedFrom":[subQ1,subQ0]});Q14=makeQuery(id+"F4.imprint","IMPRINT",FACE,{"disambiguationData":[TD([[makeQuery(id+"F4.imprint","IMPRINT",EDGE,{"disambiguationData":[TD([[subQ2,-1.0]])],"derivedFrom":subQ1}),-1.0]])]});}
            var Q15;
            {var subQ0=sQuery(id+"F4.wireOp",EDGE,"E57.MirrorC");var subQ1=sQuery(id+"F4.wireOp",EDGE,"6e4d2df1-713c-46b8-b697-84e0066bc4920.MirrorCS");var subQ2=makeQuery(id+"F4.imprint","INTERSECT",VERTEX,{"derivedFrom":[subQ1,subQ0]});Q15=makeQuery(id+"F4.imprint","IMPRINT",FACE,{"disambiguationData":[TD([[makeQuery(id+"F4.imprint","IMPRINT",EDGE,{"disambiguationData":[TD([[subQ2,-1.0]])],"derivedFrom":subQ1}),1.0]])]});}
            var Q16;
            {var subQ0=sQuery(id+"F4.wireOp",EDGE,"E49");var subQ3=sQuery(id+"F4.wireOp",EDGE,"E58.MirrorC");var subQ4=makeQuery(id+"F4.imprint","INTERSECT",VERTEX,{"derivedFrom":[subQ0,subQ3]});Q16=makeQuery(id+"F4.imprint","IMPRINT",FACE,{"disambiguationData":[TD([[makeQuery(id+"F4.imprint","IMPRINT",EDGE,{"disambiguationData":[TD([[subQ4,1.0]])],"derivedFrom":subQ3}),1.0]])]});}
            var Q17;
            {var subQ1=sQuery(id+"F4.wireOp",EDGE,"6e4d2df1-713c-46b8-b697-84e0066bc4920.MirrorCS");var subQ3=sQuery(id+"F4.wireOp",EDGE,"E58.MirrorC");var subQ4=makeQuery(id+"F4.imprint","INTERSECT",VERTEX,{"derivedFrom":[subQ1,subQ3]});Q17=makeQuery(id+"F4.imprint","IMPRINT",FACE,{"disambiguationData":[TD([[makeQuery(id+"F4.imprint","IMPRINT",EDGE,{"disambiguationData":[TD([[subQ4,1.0]])],"derivedFrom":subQ3}),1.0]])]});}
            var Q18;
            Q18=makeQuery(id+"F4.imprint","IMPRINT",FACE,{"disambiguationData":[TD([[makeQuery(id+"F4.imprint","IMPRINT",EDGE,{"derivedFrom":sQuery(id+"F4.wireOp",EDGE,"E55.MirrorC")}),-1.0]])]});
            var Q19;
            Q19=makeQuery(id+"F4.imprint","IMPRINT",FACE,{"disambiguationData":[TD([[makeQuery(id+"F4.imprint","IMPRINT",EDGE,{"derivedFrom":sQuery(id+"F4.wireOp",EDGE,"E57.MirrorC")}),1.0]])]});
            var Q20;
            Q20=makeQuery(id+"F4.imprint","IMPRINT",FACE,{"disambiguationData":[TD([[makeQuery(id+"F4.imprint","IMPRINT",EDGE,{"derivedFrom":sQuery(id+"F4.wireOp",EDGE,"E56.MirrorC")}),-1.0]])]});
            extrude(context, id + "F13", {"entities" : qUnion([Q0, Q1, Q2, Q3, Q4, Q5, Q6, Q7, Q8, Q9, Q10, Q11, Q12, Q13, Q14, Q15, Q16, Q17, Q18, Q19, Q20]), "depth" : 20 * mm});
        }
        {
            var Q0;
            {var subQ7=sQuery(id+"F4.wireOp",EDGE,"E40");Q0=makeQuery(id+"F4.imprint","IMPRINT",FACE,{"disambiguationData":[TD([[makeQuery(id+"F4.imprint","IMPRINT",EDGE,{"derivedFrom":subQ7}),-1.0]])]});}
            var Q1;
            {var subQ4=sQuery(id+"F4.wireOp",EDGE,"E43.MirrorCS");Q1=makeQuery(id+"F4.imprint","IMPRINT",FACE,{"disambiguationData":[TD([[makeQuery(id+"F4.imprint","IMPRINT",EDGE,{"derivedFrom":subQ4}),1.0]])]});}
            extrude(context, id + "F14", {"entities" : qUnion([Q0, Q1]), "operationType" : NewBodyOperationType.REMOVE, "depth" : 25 * mm});
        }
        {
            var Q0;
            Q0=sQuery(id+"F4.wireOp",VERTEX,"E47.start");
            var Q1;
            Q1=sQuery(id+"F4.wireOp",VERTEX,"E56.MirrorC.center");
            var Q2;
            Q2=sQuery(id+"F4.wireOp",VERTEX,"E57.MirrorC.center");
            var Q3;
            Q3=sQuery(id+"F4.wireOp",VERTEX,"E47.end");
            var Q4;
            Q4=sQuery(id+"F4.wireOp",VERTEX,"E59.start");
            var Q5;
            Q5=sQuery(id+"F4.wireOp",VERTEX,"E59.end");
            var Q6;
            Q6=sQuery(id+"F4.wireOp",VERTEX,"E64.start");
            var Q7;
            Q7=sQuery(id+"F4.wireOp",VERTEX,"E64.end");
            var Q8;
            Q8=makeQuery(id+"F13.opExtrude","SWEPT_BODY",BODY,{"disambiguationData":[OSD([sQuery(id+"F4.wireOp",EDGE,"E29"),sQuery(id+"F4.wireOp",EDGE,"E30"),sQuery(id+"F4.wireOp",EDGE,"E31.MirrorCS"),sQuery(id+"F4.wireOp",EDGE,"E32.MirrorCS"),sQuery(id+"F4.wireOp",EDGE,"E33.MirrorCS"),sQuery(id+"F4.wireOp",EDGE,"E34.MirrorCS"),sQuery(id+"F4.wireOp",EDGE,"E35.MirrorCS"),sQuery(id+"F4.wireOp",EDGE,"E36.MirrorCS")])]});
            hole(context, id + "F15", {"style" : HoleStyle.C_BORE, "endStyle" : HoleEndStyle.THROUGH, "oppositeDirection" : true, "holeDiameter" : 6.2 * mm, "cBoreDiameter" : 11 * mm, "cBoreDepth" : 6.2 * mm, "isTappedThrough" : true, "tappedDepth" : 12 * mm, "tapClearance" : 3, "locations" : qUnion([Q0, Q1, Q2, Q3, Q4, Q5, Q6, Q7]), "scope" : qUnion([Q8]), "startStyle" : HoleStartStyle.PART});
        }
        {
            var Q0;
            Q0=makeQuery(id+"F13.opExtrude","SWEPT_EDGE",EDGE,{"disambiguationData":[OSD([sQuery(id+"F4.wireOp",EDGE,"E31.MirrorCS"),sQuery(id+"F4.wireOp",EDGE,"E32.MirrorCS")])]});
            var Q1;
            Q1=makeQuery(id+"F13.opExtrude","SWEPT_EDGE",EDGE,{"disambiguationData":[OSD([sQuery(id+"F4.wireOp",EDGE,"E35.MirrorCS"),sQuery(id+"F4.wireOp",EDGE,"E36.MirrorCS")])]});
            var Q2;
            Q2=makeQuery(id+"F13.opExtrude","SWEPT_EDGE",EDGE,{"disambiguationData":[OSD([sQuery(id+"F4.wireOp",EDGE,"E29"),sQuery(id+"F4.wireOp",EDGE,"E30")])]});
            var Q3;
            Q3=makeQuery(id+"F13.opExtrude","SWEPT_EDGE",EDGE,{"disambiguationData":[OSD([sQuery(id+"F4.wireOp",EDGE,"E33.MirrorCS"),sQuery(id+"F4.wireOp",EDGE,"E34.MirrorCS")])]});
            fillet(context, id + "F16", {"entities" : qUnion([Q0, Q1, Q2, Q3]), "radius" : 5 * mm, "tangentPropagation" : true, "allowEdgeOverflow" : false});
        }
        {
            var Q0;
            Q0=sQuery(id+"F0.wireOp",VERTEX,"E25.start");
            var Q1;
            Q1=sQuery(id+"F0.wireOp",VERTEX,"E25.end");
            var Q2;
            Q2=makeQuery(id+"F1.opExtrude","SWEPT_BODY",BODY,{"disambiguationData":[OSD([sQuery(id+"F0.wireOp",EDGE,"E0"),sQuery(id+"F0.wireOp",EDGE,"E1"),sQuery(id+"F0.wireOp",EDGE,"E2"),sQuery(id+"F0.wireOp",EDGE,"E3"),sQuery(id+"F0.wireOp",EDGE,"E7")])]});
            hole(context, id + "F17", {"style" : HoleStyle.SIMPLE, "endStyle" : HoleEndStyle.THROUGH, "holeDiameter" : 6.2 * mm, "isTappedThrough" : true, "tappedDepth" : 12 * mm, "tapClearance" : 3, "locations" : qUnion([Q0, Q1]), "scope" : qUnion([Q2]), "startStyle" : HoleStartStyle.PART});
        }
    });
